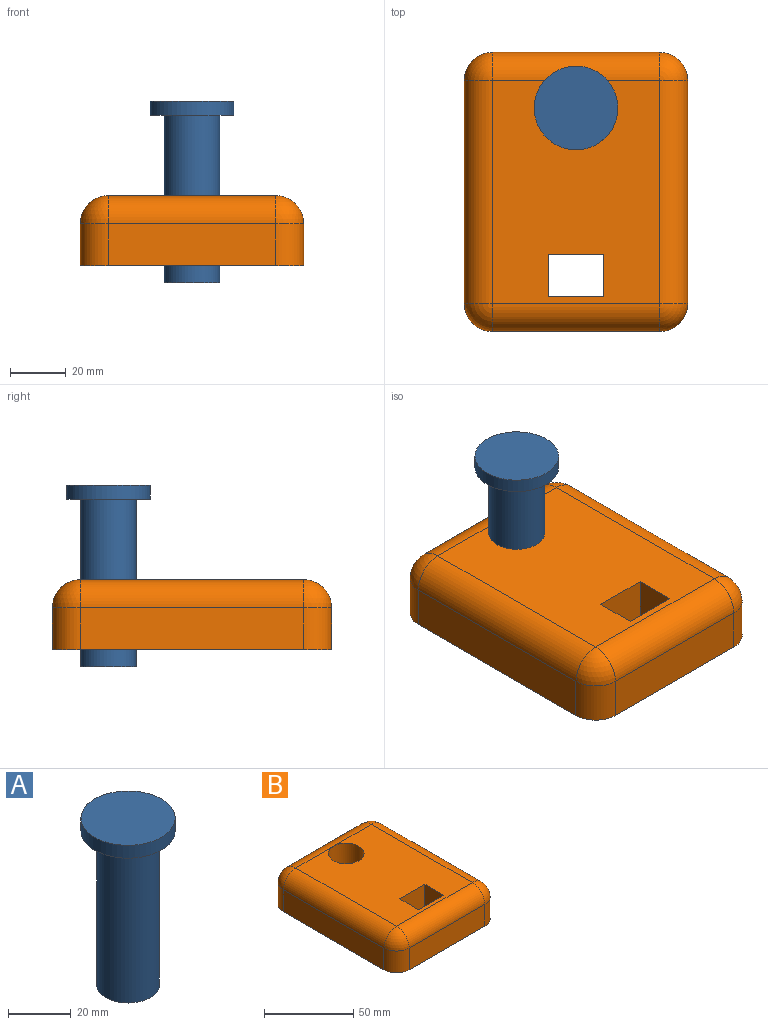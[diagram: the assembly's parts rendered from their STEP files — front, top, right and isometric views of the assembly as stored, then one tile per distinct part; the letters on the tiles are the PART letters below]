
ASSEMBLY  parts=2 mates=1
PART A: 5 faces, bbox 30x30x65 mm
  f0: cylinder r=10mm len=60mm, axis (0,0,-1), area 3769.9mm2, adj f1,f4
  f1: plane 20x20mm, normal (0,0,-1), area 314.2mm2, adj f0
  f2: cylinder r=15mm len=30mm, axis (0,0,-1), area 471.2mm2, adj f3,f4
  f3: plane 30x30mm, normal (0,0,1), area 706.9mm2, adj f2
  f4: plane 30x30mm, normal (0,0,-1), area 392.7mm2, adj f0,f2
PART B: 23 faces, bbox 80x100x25 mm
  f0: plane 80x60mm, normal (0,0,1), area 4185.8mm2, adj f9,f10,f14,f15,f18,f19,f20,f21
  f1: plane 100x80mm, normal (0,0,-1), area 7300mm2, adj f2,f3,f4,f5,f6,f8,f11,f17
  f2: plane 80x15mm, normal (1,0,0), area 1200mm2, adj f1,f8,f14,f17
  f3: plane 60x15mm, normal (0,1,0), area 900mm2, adj f1,f11,f15,f17
  f4: plane 80x15mm, normal (-1,0,0), area 1200mm2, adj f1,f6,f10,f11
  f5: plane 60x15mm, normal (0,-1,0), area 900mm2, adj f1,f6,f8,f9
  f6: cylinder r=10mm len=15mm, axis (0,0,1), area 235.6mm2, adj f1,f4,f5,f7
  f7: sphere r=10mm, area 157.1mm2, adj f6,f9,f10
  f8: cylinder r=10mm len=15mm, axis (0,0,-1), area 235.6mm2, adj f1,f2,f5,f12
  f9: cylinder r=10mm len=60mm, axis (-1,0,0), area 942.5mm2, adj f0,f5,f7,f12
  f10: cylinder r=10mm len=80mm, axis (0,1,0), area 1256.6mm2, adj f0,f4,f7,f13
  f11: cylinder r=10mm len=15mm, axis (0,0,-1), area 235.6mm2, adj f1,f3,f4,f13
  f12: sphere r=10mm, area 157.1mm2, adj f8,f9,f14
  f13: sphere r=10mm, area 157.1mm2, adj f10,f11,f15
  f14: cylinder r=10mm len=80mm, axis (0,-1,0), area 1256.6mm2, adj f0,f2,f12,f16
  f15: cylinder r=10mm len=60mm, axis (1,0,0), area 942.5mm2, adj f0,f3,f13,f16
  f16: sphere r=10mm, area 157.1mm2, adj f14,f15,f17
  f17: cylinder r=10mm len=15mm, axis (0,0,1), area 235.6mm2, adj f1,f2,f3,f16
  f18: plane 25x15mm, normal (-1,0,0), area 375mm2, adj f0,f1,f19,f21
  f19: plane 25x20mm, normal (0,-1,0), area 500mm2, adj f0,f1,f18,f20
  f20: plane 25x15mm, normal (1,0,0), area 375mm2, adj f0,f1,f19,f21
  f21: plane 25x20mm, normal (0,1,0), area 500mm2, adj f0,f1,f18,f20
  f22: cylinder r=10mm len=25mm, axis (0,0,1), area 1570.8mm2, adj f0,f1
PLACE A rot(axis=(0,0,1),107.2deg) t=(0,30.1,-1.15)mm
PLACE B t=(0,0.1,-25)mm
MATE cylindrical A.f0 <-> B.f22  axis (0,0,-1) through (0,30.1,28.85)mm
